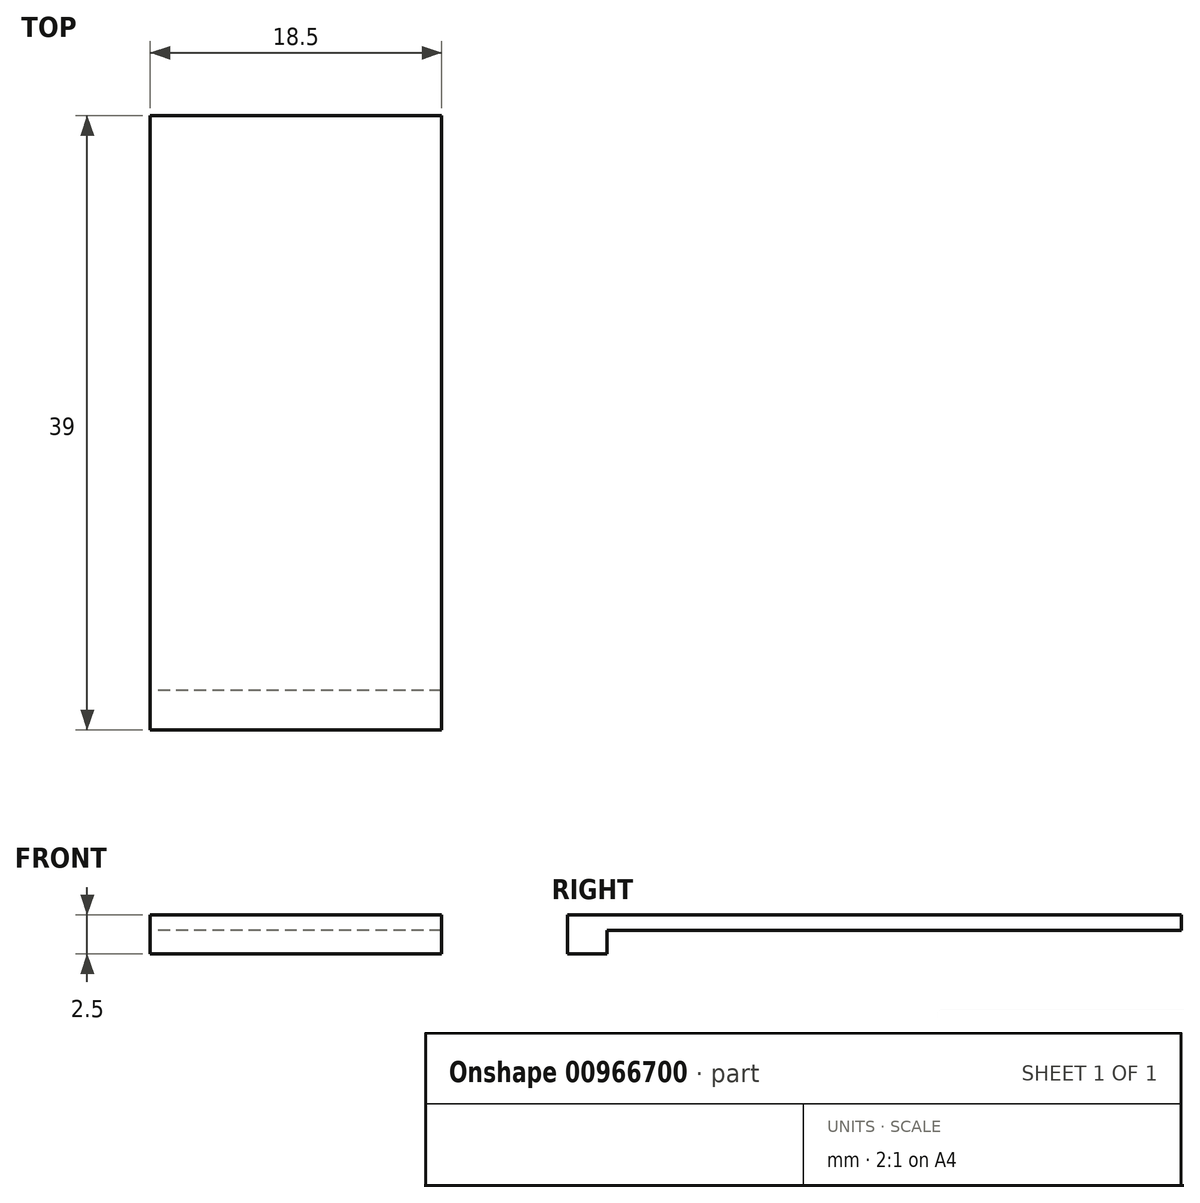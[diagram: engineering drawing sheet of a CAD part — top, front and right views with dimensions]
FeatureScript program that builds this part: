
annotation { "Feature Type Name" : "Feature", "Feature Type Description" : "" }
export const myFeature = defineFeature(function(context is Context, id is Id, definition is map)
    precondition{}
    {
        {
            var Q0;
            Q0=qCreatedBy(makeId("Top.planeOp"),FACE);
            var sketch = newSketch(context, id + "F0", { "sketchPlane" : qUnion([Q0])});
            skLineSegment(sketch, "E0.bottom", {"start": v(9.25, 19.5) * mm, "end": v(-9.25, 19.5) * mm});
            skLineSegment(sketch, "E0.top", {"start": v(9.25, -19.5) * mm, "end": v(-9.25, -19.5) * mm});
            skLineSegment(sketch, "E0.left", {"start": v(9.25, 19.5) * mm, "end": v(9.25, -19.5) * mm});
            skLineSegment(sketch, "E0.right", {"start": v(-9.25, 19.5) * mm, "end": v(-9.25, -19.5) * mm});
            skPoint(sketch, "E0.middle", {"position": v(0, 0) * mm});
            skSolve(sketch);
        }
        {
            var Q0;
            Q0 = qSketchRegion(id + "F0", true);
            extrude(context, id + "F1", {"entities" : qUnion([Q0]), "endBound" : BoundingType.SYMMETRIC, "depth" : 1 * mm, "offsetDistance" : 25 * mm});
        }
        {
            var Q0;
            Q0=makeQuery(id+"F1.opExtrude","CAP_FACE",FACE,{"disambiguationData":[OSD([sQuery(id+"F0.wireOp",EDGE,"E0.bottom"),sQuery(id+"F0.wireOp",EDGE,"E0.top"),sQuery(id+"F0.wireOp",EDGE,"E0.left"),sQuery(id+"F0.wireOp",EDGE,"E0.right")])],"isStart":true});
            var sketch = newSketch(context, id + "F2", { "sketchPlane" : qUnion([Q0])});
            skLineSegment(sketch, "E1.bottom", {"start": v(9.25, 19.5) * mm, "end": v(-9.25, 19.5) * mm});
            skLineSegment(sketch, "E1.top", {"start": v(9.25, 17) * mm, "end": v(-9.25, 17) * mm});
            skLineSegment(sketch, "E1.left", {"start": v(9.25, 19.5) * mm, "end": v(9.25, 17) * mm});
            skLineSegment(sketch, "E1.right", {"start": v(-9.25, 19.5) * mm, "end": v(-9.25, 17) * mm});
            skSolve(sketch);
        }
        {
            var Q0;
            Q0 = qSketchRegion(id + "F2", true);
            extrude(context, id + "F3", {"entities" : qUnion([Q0]), "operationType" : NewBodyOperationType.ADD, "depth" : 1.5 * mm, "offsetDistance" : 25 * mm});
        }
    });
